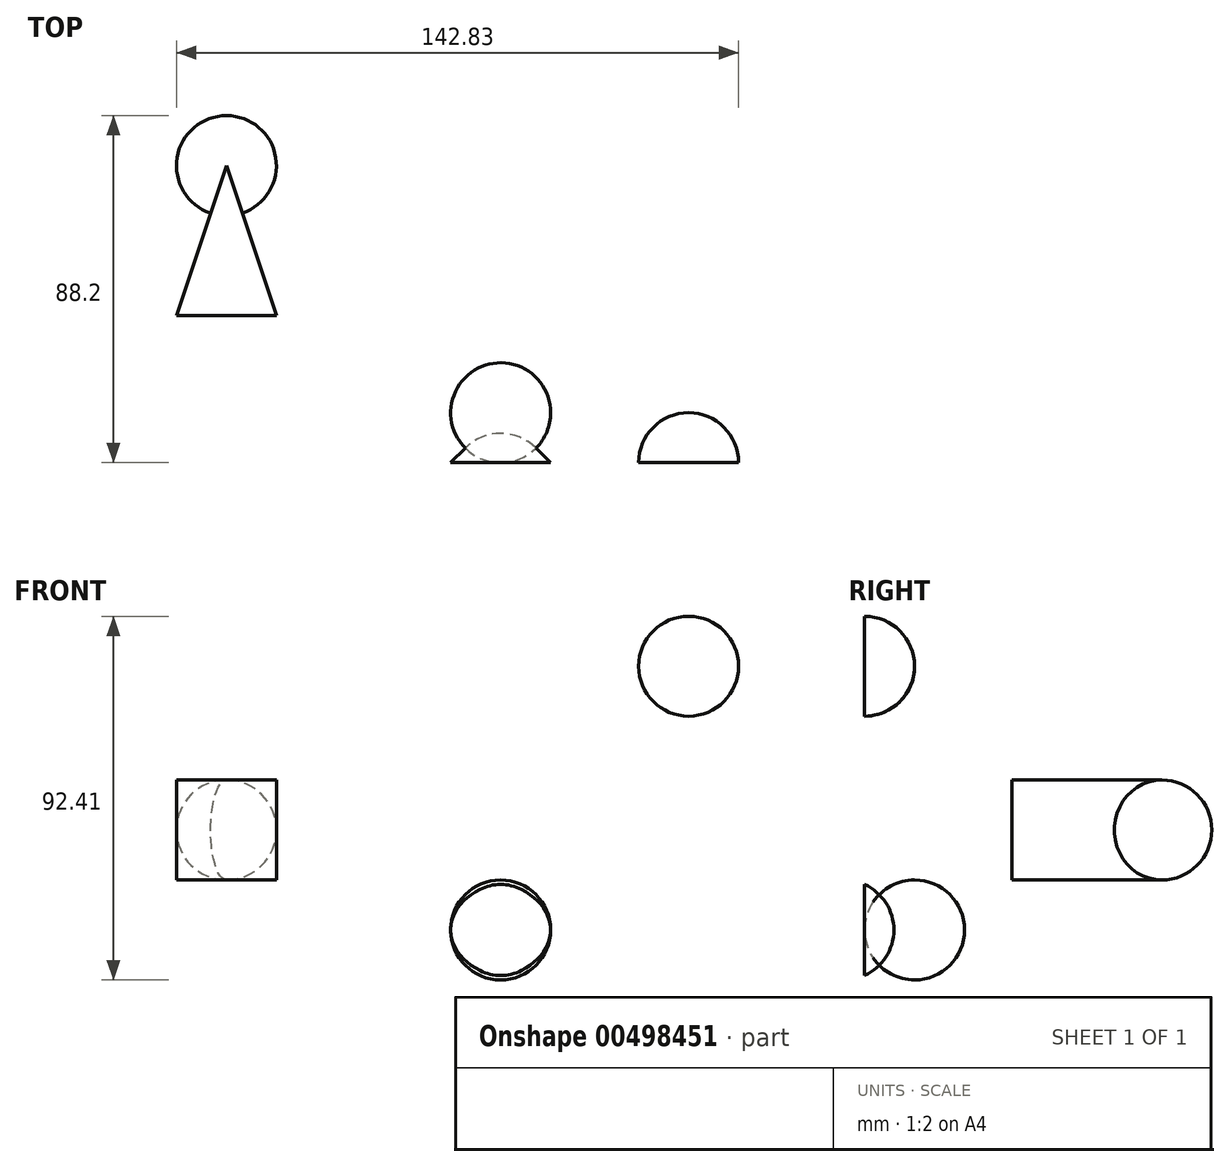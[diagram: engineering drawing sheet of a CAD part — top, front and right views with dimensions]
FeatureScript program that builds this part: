
annotation { "Feature Type Name" : "Feature", "Feature Type Description" : "" }
export const myFeature = defineFeature(function(context is Context, id is Id, definition is map)
    precondition{}
    {
        {
            var Q0;
            Q0=qCreatedBy(makeId("Top.planeOp"),FACE);
            var sketch = newSketch(context, id + "F0", { "sketchPlane" : qUnion([Q0])});
            skArc(sketch, "E0", {"start": v(8.98, -8.98) * mm, "mid": v(0, 12.7) * mm, "end": v(-8.98, -8.98) * mm});
            skLineSegment(sketch, "E1", {"start": v(-8.98, -8.98) * mm, "end": v(-12.7, -12.7) * mm});
            skLineSegment(sketch, "E2", {"start": v(-12.7, -12.7) * mm, "end": v(12.7, -12.7) * mm});
            skLineSegment(sketch, "E3", {"start": v(12.7, -12.7) * mm, "end": v(8.98, -8.98) * mm});
            skCircle(sketch, "E4", {"center": v(0, 0) * mm, "radius": 12.7 * mm});
            skLineSegment(sketch, "E5", {"start": v(-8.98, -8.98) * mm, "end": v(0, 0) * mm});
            skLineSegment(sketch, "E6", {"start": v(0, 0) * mm, "end": v(8.98, -8.98) * mm});
            skArc(sketch, "E7", {"start": v(-60.7, 53.82) * mm, "mid": v(-69.67, 75.5) * mm, "end": v(-78.65, 53.82) * mm});
            skCircle(sketch, "E8", {"center": v(-69.67, 62.8) * mm, "radius": 12.7 * mm});
            skLineSegment(sketch, "E9", {"start": v(-82.37, 24.7) * mm, "end": v(-56.97, 24.7) * mm});
            skLineSegment(sketch, "E10", {"start": v(-82.37, 24.7) * mm, "end": v(-69.67, 62.8) * mm});
            skLineSegment(sketch, "E11", {"start": v(-69.67, 62.8) * mm, "end": v(-56.97, 24.7) * mm});
            skSolve(sketch);
        }
        {
            var Q0;
            {var subQ0=sQuery(id+"F0.wireOp",EDGE,"E4");var subQ1=makeQuery(id+"F0.imprint","INTERSECT",VERTEX,{"derivedFrom":[sQuery(id+"F0.wireOp",EDGE,"E1"),subQ0]});Q0=makeQuery(id+"F0.imprint","IMPRINT",FACE,{"disambiguationData":[TD([[makeQuery(id+"F0.imprint","IMPRINT",EDGE,{"disambiguationData":[TD([[subQ1,-1.0]])],"derivedFrom":subQ0}),1.0]])]});}
            var Q1;
            {var subQ0=sQuery(id+"F0.wireOp",EDGE,"E5");Q1=makeQuery(id+"F0.imprint","IMPRINT",FACE,{"disambiguationData":[TD([[makeQuery(id+"F0.imprint","IMPRINT",EDGE,{"derivedFrom":subQ0}),1.0]])]});}
            extrude(context, id + "F1", {"entities" : qUnion([Q0, Q1]), "oppositeDirection" : true, "depth" : 25.4 * mm});
        }
        {
            var Q0;
            Q0=makeQuery(id+"F1.opExtrude","CAP_FACE",FACE,{"disambiguationData":[OSD([sQuery(id+"F0.wireOp",EDGE,"E4")])],"isStart":false});
            var Q1;
            Q1=makeQuery(id+"F1.opExtrude","CAP_FACE",FACE,{"disambiguationData":[OSD([sQuery(id+"F0.wireOp",EDGE,"E4")])],"isStart":true});
            fillet(context, id + "F2", {"entities" : qUnion([Q0, Q1]), "radius" : 12.7 * mm, "tangentPropagation" : true, "allowEdgeOverflow" : false});
        }
        {
            var Q0;
            {var subQ0=sQuery(id+"F0.wireOp",EDGE,"E5");Q0=makeQuery(id+"F0.imprint","IMPRINT",FACE,{"disambiguationData":[TD([[makeQuery(id+"F0.imprint","IMPRINT",EDGE,{"derivedFrom":subQ0}),-1.0]])]});}
            var Q1;
            {var subQ0=sQuery(id+"F0.wireOp",EDGE,"E1");Q1=makeQuery(id+"F0.imprint","IMPRINT",FACE,{"disambiguationData":[TD([[makeQuery(id+"F0.imprint","IMPRINT",EDGE,{"derivedFrom":subQ0}),1.0]])]});}
            var Q2;
            {var subQ0=sQuery(id+"F0.wireOp",EDGE,"E3");Q2=makeQuery(id+"F0.imprint","IMPRINT",FACE,{"disambiguationData":[TD([[makeQuery(id+"F0.imprint","IMPRINT",EDGE,{"derivedFrom":subQ0}),1.0]])]});}
            extrude(context, id + "F3", {"entities" : qUnion([Q0, Q1, Q2]), "oppositeDirection" : true, "depth" : 25.4 * mm});
        }
        {
            var Q0;
            Q0=makeQuery(id+"F3.opExtrude","CAP_EDGE",EDGE,{"disambiguationData":[OSD([sQuery(id+"F0.wireOp",EDGE,"E3"),sQuery(id+"F0.wireOp",EDGE,"E6")])],"isStart":true});
            var Q1;
            Q1=makeQuery(id+"F3.opExtrude","CAP_EDGE",EDGE,{"disambiguationData":[OSD([sQuery(id+"F0.wireOp",EDGE,"E3"),sQuery(id+"F0.wireOp",EDGE,"E6")])],"isStart":false});
            fillet(context, id + "F4", {"entities" : qUnion([Q0, Q1]), "radius" : 12.7 * mm, "tangentPropagation" : true, "allowEdgeOverflow" : false});
        }
        {
            var Q0;
            Q0=makeQuery(id+"F3.opExtrude","CAP_EDGE",EDGE,{"disambiguationData":[OSD([sQuery(id+"F0.wireOp",EDGE,"E1"),sQuery(id+"F0.wireOp",EDGE,"E5")])],"isStart":true});
            var Q1;
            Q1=makeQuery(id+"F4.opFillet","BLEND_EDGE",EDGE,{"blendedFrom":[makeQuery(id+"F3.opExtrude","CAP_EDGE",EDGE,{"disambiguationData":[OSD([sQuery(id+"F0.wireOp",EDGE,"E3"),sQuery(id+"F0.wireOp",EDGE,"E6")])],"isStart":false}),makeQuery(id+"F3.opExtrude","SWEPT_FACE",FACE,{"disambiguationData":[OSD([sQuery(id+"F0.wireOp",EDGE,"E1"),sQuery(id+"F0.wireOp",EDGE,"E5")])]})],"blendedInto":[makeQuery(id+"F3.opExtrude","SWEPT_FACE",FACE,{"disambiguationData":[OSD([sQuery(id+"F0.wireOp",EDGE,"E1"),sQuery(id+"F0.wireOp",EDGE,"E5")])]})]});
            var Q2;
            Q2=makeQuery(id+"F3.opExtrude","CAP_EDGE",EDGE,{"disambiguationData":[OSD([sQuery(id+"F0.wireOp",EDGE,"E1"),sQuery(id+"F0.wireOp",EDGE,"E5")])],"isStart":false});
            fillet(context, id + "F5", {"entities" : qUnion([Q0, Q1, Q2]), "radius" : 12.7 * mm, "tangentPropagation" : true, "allowEdgeOverflow" : false});
        }
        {
            var Q0;
            Q0=qCreatedBy(makeId("Front.planeOp"),FACE);
            var sketch = newSketch(context, id + "F6", { "sketchPlane" : qUnion([Q0])});
            skCircle(sketch, "E12", {"center": v(47.76, 54.3) * mm, "radius": 12.7 * mm});
            skSolve(sketch);
        }
        {
            var Q0;
            Q0 = qSketchRegion(id + "F6", true);
            extrude(context, id + "F7", {"entities" : qUnion([Q0]), "depth" : 12.7 * mm});
        }
        {
            var Q0;
            Q0=makeQuery(id+"F7.opExtrude","CAP_FACE",FACE,{"disambiguationData":[OSD([sQuery(id+"F6.wireOp",EDGE,"E12")])],"isStart":true});
            fillet(context, id + "F8", {"entities" : qUnion([Q0]), "radius" : 12.7 * mm, "tangentPropagation" : true, "allowEdgeOverflow" : false});
        }
        {
            var Q0;
            {var subQ3=sQuery(id+"F0.wireOp",EDGE,"E8");var subQ5=makeQuery(id+"F0.imprint","IMPRINT",VERTEX,{"disambiguationData":[OD(0.0)],"derivedFrom":subQ3});Q0=makeQuery(id+"F0.imprint","IMPRINT",FACE,{"disambiguationData":[TD([[makeQuery(id+"F0.imprint","IMPRINT",EDGE,{"disambiguationData":[TD([[subQ5,1.0]])],"derivedFrom":subQ3}),1.0]])]});}
            var Q1;
            {var subQ0=sQuery(id+"F0.wireOp",EDGE,"E10");var subQ1=sQuery(id+"F0.wireOp",EDGE,"E8");var subQ2=makeQuery(id+"F0.imprint","INTERSECT",VERTEX,{"derivedFrom":[subQ1,subQ0]});Q1=makeQuery(id+"F0.imprint","IMPRINT",FACE,{"disambiguationData":[TD([[makeQuery(id+"F0.imprint","IMPRINT",EDGE,{"disambiguationData":[TD([[subQ2,-1.0]])],"derivedFrom":subQ1}),1.0]])]});}
            extrude(context, id + "F9", {"entities" : qUnion([Q0, Q1]), "depth" : 25.4 * mm});
        }
        {
            var Q0;
            Q0=makeQuery(id+"F9.opExtrude","CAP_FACE",FACE,{"disambiguationData":[OSD([sQuery(id+"F0.wireOp",EDGE,"E8")])],"isStart":false});
            var Q1;
            Q1=makeQuery(id+"F9.opExtrude","CAP_FACE",FACE,{"disambiguationData":[OSD([sQuery(id+"F0.wireOp",EDGE,"E8")])],"isStart":true});
            fillet(context, id + "F10", {"entities" : qUnion([Q0, Q1]), "radius" : 12.7 * mm, "tangentPropagation" : true, "allowEdgeOverflow" : false});
        }
        {
            var Q0;
            {var subQ0=sQuery(id+"F0.wireOp",EDGE,"E10");var subQ1=sQuery(id+"F0.wireOp",EDGE,"E8");var subQ2=makeQuery(id+"F0.imprint","INTERSECT",VERTEX,{"derivedFrom":[subQ1,subQ0]});Q0=makeQuery(id+"F0.imprint","IMPRINT",FACE,{"disambiguationData":[TD([[makeQuery(id+"F0.imprint","IMPRINT",EDGE,{"disambiguationData":[TD([[subQ2,-1.0]])],"derivedFrom":subQ1}),1.0]])]});}
            var Q1;
            {var subQ5=sQuery(id+"F0.wireOp",EDGE,"E9");Q1=makeQuery(id+"F0.imprint","IMPRINT",FACE,{"disambiguationData":[TD([[makeQuery(id+"F0.imprint","IMPRINT",EDGE,{"derivedFrom":subQ5}),1.0]])]});}
            extrude(context, id + "F11", {"entities" : qUnion([Q0, Q1]), "operationType" : NewBodyOperationType.ADD, "depth" : 25.4 * mm});
        }
    });
